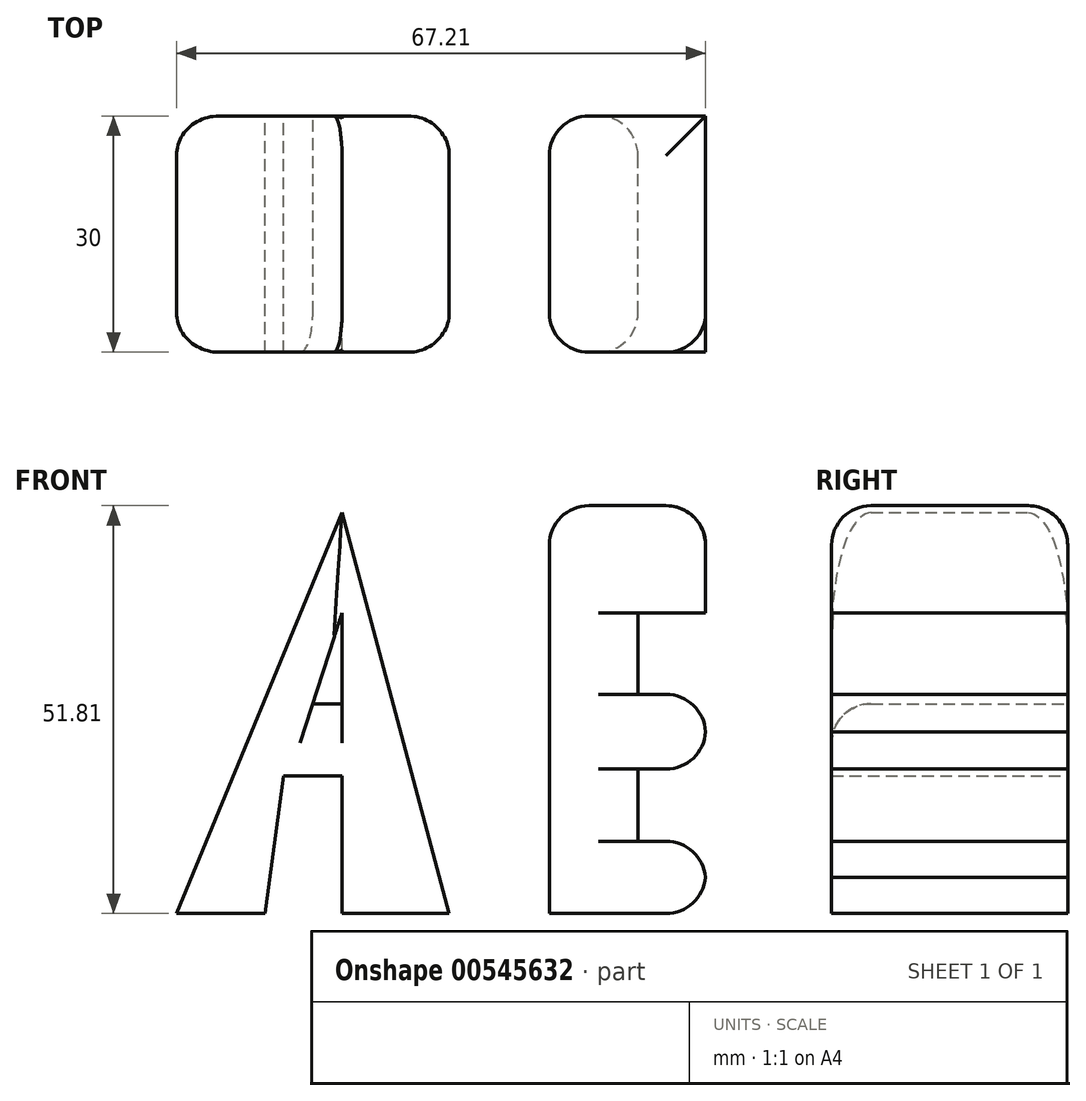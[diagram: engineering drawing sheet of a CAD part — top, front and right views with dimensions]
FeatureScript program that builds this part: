
annotation { "Feature Type Name" : "Feature", "Feature Type Description" : "" }
export const myFeature = defineFeature(function(context is Context, id is Id, definition is map)
    precondition{}
    {
        {
            var Q0;
            Q0=qCreatedBy(makeId("Front.planeOp"),FACE);
            var sketch = newSketch(context, id + "F0", { "sketchPlane" : qUnion([Q0])});
            skLineSegment(sketch, "E0", {"start": v(-58.62, 0) * mm, "end": v(-37.6, 50.92) * mm});
            skLineSegment(sketch, "E1", {"start": v(-23.98, 0) * mm, "end": v(-37.6, 50.92) * mm});
            skLineSegment(sketch, "E2", {"start": v(-23.98, 0) * mm, "end": v(-37.6, 0) * mm});
            skLineSegment(sketch, "E3", {"start": v(-58.62, 0) * mm, "end": v(-47.37, 0) * mm});
            skPoint(sketch, "E4.end.orphan", {"position": v(-37.6, 17.47) * mm});
            skPoint(sketch, "E5.end.orphan", {"position": v(-45, 17.47) * mm});
            skLineSegment(sketch, "E6", {"start": v(-47.37, 0) * mm, "end": v(-45, 17.47) * mm});
            skLineSegment(sketch, "E7", {"start": v(-37.6, 0) * mm, "end": v(-37.6, 17.47) * mm});
            skLineSegment(sketch, "E8", {"start": v(-37.6, 17.47) * mm, "end": v(-45, 17.47) * mm});
            skLineSegment(sketch, "E9", {"start": v(-41.3, 26.64) * mm, "end": v(-37.6, 38.2) * mm});
            skPoint(sketch, "E9.startSnap0", {"position": v(-41.3, 17.47) * mm});
            skLineSegment(sketch, "E10", {"start": v(-41.3, 26.64) * mm, "end": v(-37.6, 26.64) * mm});
            skLineSegment(sketch, "E11", {"start": v(-37.6, 26.64) * mm, "end": v(-37.6, 38.2) * mm});
            skLineSegment(sketch, "E12", {"start": v(-11.25, 0) * mm, "end": v(-11.25, 51.8) * mm});
            skPoint(sketch, "E12.startSnap0", {"position": v(-53, 0) * mm});
            skLineSegment(sketch, "E13", {"start": v(-11.25, 51.8) * mm, "end": v(8.59, 51.8) * mm});
            skPoint(sketch, "E14.start.orphan", {"position": v(8.59, 45) * mm});
            skPoint(sketch, "E15.end.orphan", {"position": v(8.59, 38.2) * mm});
            skPoint(sketch, "E16.orphan", {"position": v(8.59, 49.14) * mm});
            skLineSegment(sketch, "E17", {"start": v(8.59, 38.2) * mm, "end": v(8.59, 51.8) * mm});
            skLineSegment(sketch, "E18", {"start": v(8.59, 38.2) * mm, "end": v(0, 38.2) * mm});
            skLineSegment(sketch, "E19", {"start": v(0, 38.2) * mm, "end": v(0, 27.83) * mm});
            skLineSegment(sketch, "E20", {"start": v(0, 27.83) * mm, "end": v(8.59, 27.83) * mm});
            skLineSegment(sketch, "E21", {"start": v(8.59, 27.83) * mm, "end": v(8.59, 18.36) * mm});
            skLineSegment(sketch, "E22", {"start": v(8.59, 18.36) * mm, "end": v(0, 18.36) * mm});
            skLineSegment(sketch, "E23", {"start": v(0, 18.36) * mm, "end": v(0, 9.18) * mm});
            skLineSegment(sketch, "E24", {"start": v(0, 9.18) * mm, "end": v(8.59, 9.18) * mm});
            skLineSegment(sketch, "E25", {"start": v(8.59, 0) * mm, "end": v(-11.25, 0) * mm});
            skLineSegment(sketch, "E26", {"start": v(8.59, 9.18) * mm, "end": v(8.59, 0) * mm});
            skSolve(sketch);
        }
        {
            var Q0;
            Q0=makeQuery(id+"F0.imprint","IMPRINT",FACE,{"disambiguationData":[TD([[makeQuery(id+"F0.imprint","IMPRINT",EDGE,{"derivedFrom":sQuery(id+"F0.wireOp",EDGE,"E0")}),-1.0]])]});
            var Q1;
            Q1=makeQuery(id+"F0.imprint","IMPRINT",FACE,{"disambiguationData":[TD([[makeQuery(id+"F0.imprint","IMPRINT",EDGE,{"derivedFrom":sQuery(id+"F0.wireOp",EDGE,"E12")}),-1.0]])]});
            extrude(context, id + "F1", {"entities" : qUnion([Q0, Q1]), "depth" : 30 * mm, "offsetDistance" : 25 * mm});
        }
        {
            var Q0;
            Q0=makeQuery(id+"F1.opExtrude","CAP_EDGE",EDGE,{"disambiguationData":[OSD([sQuery(id+"F0.wireOp",EDGE,"E0")])],"isStart":false});
            var Q1;
            Q1=makeQuery(id+"F1.opExtrude","CAP_EDGE",EDGE,{"disambiguationData":[OSD([sQuery(id+"F0.wireOp",EDGE,"E0")])],"isStart":true});
            var Q2;
            Q2=makeQuery(id+"F1.opExtrude","CAP_EDGE",EDGE,{"disambiguationData":[OSD([sQuery(id+"F0.wireOp",EDGE,"E1")])],"isStart":false});
            var Q3;
            Q3=makeQuery(id+"F1.opExtrude","CAP_EDGE",EDGE,{"disambiguationData":[OSD([sQuery(id+"F0.wireOp",EDGE,"E1")])],"isStart":true});
            var Q4;
            Q4=makeQuery(id+"F1.opExtrude","CAP_EDGE",EDGE,{"disambiguationData":[OSD([sQuery(id+"F0.wireOp",EDGE,"E12")])],"isStart":true});
            var Q5;
            Q5=makeQuery(id+"F1.opExtrude","CAP_EDGE",EDGE,{"disambiguationData":[OSD([sQuery(id+"F0.wireOp",EDGE,"E13")])],"isStart":true});
            var Q6;
            Q6=makeQuery(id+"F1.opExtrude","CAP_EDGE",EDGE,{"disambiguationData":[OSD([sQuery(id+"F0.wireOp",EDGE,"E13")])],"isStart":false});
            var Q7;
            Q7=makeQuery(id+"F1.opExtrude","SWEPT_EDGE",EDGE,{"disambiguationData":[OSD([sQuery(id+"F0.wireOp",EDGE,"E12"),sQuery(id+"F0.wireOp",EDGE,"E13")])]});
            var Q8;
            Q8=makeQuery(id+"F1.opExtrude","CAP_EDGE",EDGE,{"disambiguationData":[OSD([sQuery(id+"F0.wireOp",EDGE,"E12")])],"isStart":false});
            var Q9;
            Q9=makeQuery(id+"F1.opExtrude","CAP_EDGE",EDGE,{"disambiguationData":[OSD([sQuery(id+"F0.wireOp",EDGE,"E17")])],"isStart":false});
            var Q10;
            Q10=makeQuery(id+"F1.opExtrude","SWEPT_EDGE",EDGE,{"disambiguationData":[OSD([sQuery(id+"F0.wireOp",EDGE,"E13"),sQuery(id+"F0.wireOp",EDGE,"E17")])]});
            var Q11;
            Q11=makeQuery(id+"F1.opExtrude","SWEPT_EDGE",EDGE,{"disambiguationData":[OSD([sQuery(id+"F0.wireOp",EDGE,"E20"),sQuery(id+"F0.wireOp",EDGE,"E21")])]});
            var Q12;
            Q12=makeQuery(id+"F1.opExtrude","SWEPT_EDGE",EDGE,{"disambiguationData":[OSD([sQuery(id+"F0.wireOp",EDGE,"E21"),sQuery(id+"F0.wireOp",EDGE,"E22")])]});
            var Q13;
            Q13=makeQuery(id+"F1.opExtrude","SWEPT_EDGE",EDGE,{"disambiguationData":[OSD([sQuery(id+"F0.wireOp",EDGE,"E24"),sQuery(id+"F0.wireOp",EDGE,"E26")])]});
            var Q14;
            Q14=makeQuery(id+"F1.opExtrude","SWEPT_EDGE",EDGE,{"disambiguationData":[OSD([sQuery(id+"F0.wireOp",EDGE,"E25"),sQuery(id+"F0.wireOp",EDGE,"E26")])]});
            fillet(context, id + "F2", {"entities" : qUnion([Q0, Q1, Q2, Q3, Q4, Q5, Q6, Q7, Q8, Q9, Q10, Q11, Q12, Q13, Q14]), "radius" : 5 * mm, "tangentPropagation" : true, "allowEdgeOverflow" : false});
        }
        {
            var Q0;
            Q0=makeQuery(id+"F1.opExtrude","CAP_EDGE",EDGE,{"disambiguationData":[OSD([sQuery(id+"F0.wireOp",EDGE,"E19")])],"isStart":true});
            var Q1;
            Q1=makeQuery(id+"F1.opExtrude","CAP_EDGE",EDGE,{"disambiguationData":[OSD([sQuery(id+"F0.wireOp",EDGE,"E23")])],"isStart":true});
            var Q2;
            Q2=makeQuery(id+"F1.opExtrude","CAP_EDGE",EDGE,{"disambiguationData":[OSD([sQuery(id+"F0.wireOp",EDGE,"E23")])],"isStart":false});
            var Q3;
            Q3=makeQuery(id+"F1.opExtrude","CAP_EDGE",EDGE,{"disambiguationData":[OSD([sQuery(id+"F0.wireOp",EDGE,"E19")])],"isStart":false});
            var Q4;
            Q4=makeQuery(id+"F1.opExtrude","CAP_EDGE",EDGE,{"disambiguationData":[OSD([sQuery(id+"F0.wireOp",EDGE,"E10")])],"isStart":false});
            fillet(context, id + "F3", {"entities" : qUnion([Q0, Q1, Q2, Q3, Q4]), "radius" : 5 * mm, "tangentPropagation" : true, "allowEdgeOverflow" : false});
        }
    });
